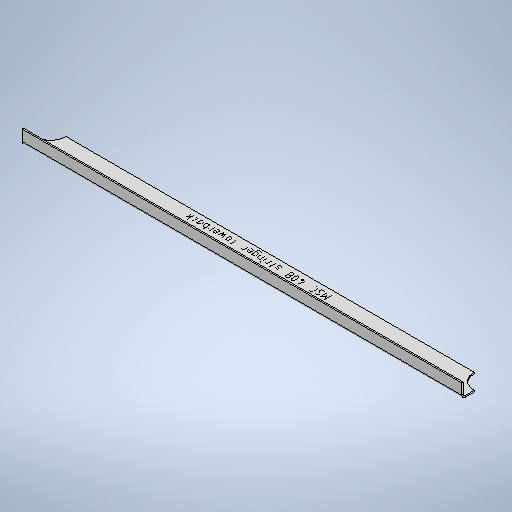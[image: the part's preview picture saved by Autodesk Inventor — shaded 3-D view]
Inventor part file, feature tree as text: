
AUTODESK INVENTOR PART (.ipt)
format: ipt  version: 2025 (Build 290162010, 162A)  size: 449,536 bytes
history: native  units: mm
features: other x5, sheet_metal_op x4, sketch x4, extrude x1, mirror x1
ambient origin geometry x8: Origin, YZ Plane, XZ Plane, XY Plane, X Axis, Y Axis, Z Axis, Center Point
bodies: Solid1 (feature_tree)
feature tree (15):
  sheet_metal_op  "Face1"
  sheet_metal_op  "Flange1"
  extrude  "Extrusion2"  Depth=2.0mm
  other  "Mark2"
  other  "A-Side Definition"
  mirror  "Mirror3"
  sketch  "Sketch1"  dims[d1=40.0mm d2=2.0mm]
  other  "Plate1"
  sketch  "Sketch2"  dims[d3=2.0mm]
  other  "Plate2"
  sheet_metal_op  "Bend1"
  sheet_metal_op  "Corner1"
  sketch  "Sketch6"  dims[d4=1.0mm]
  sketch  "Sketch9"  dims[d5=4.0mm d6=2.75mm d7=20.0mm d8=90.0deg d9=2.75mm d10=8.0mm d11=2.0mm d12=2.75mm d24=45.0mm d25=30.0mm d26=0.0mm d40=200.0mm d41=12.0mm d42=5.0mm d43=5.0mm d45=625.0mm]
  other  "Definition1"
